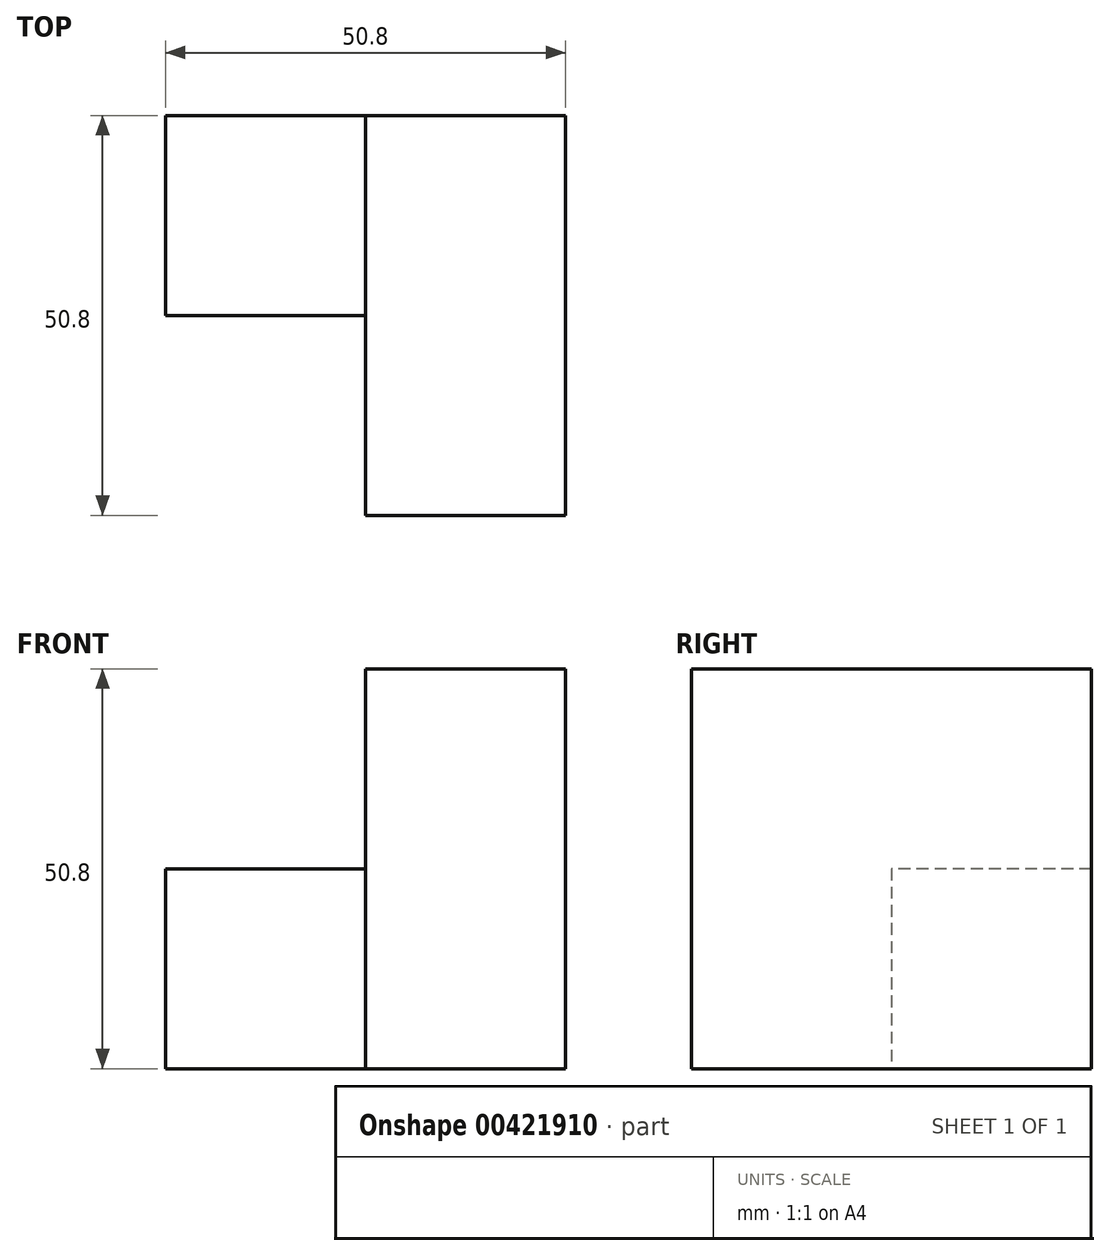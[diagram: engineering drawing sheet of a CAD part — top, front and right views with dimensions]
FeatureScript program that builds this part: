
annotation { "Feature Type Name" : "Feature", "Feature Type Description" : "" }
export const myFeature = defineFeature(function(context is Context, id is Id, definition is map)
    precondition{}
    {
        {
            var Q0;
            Q0=qCreatedBy(makeId("Front.planeOp"),FACE);
            var sketch = newSketch(context, id + "F0", { "sketchPlane" : qUnion([Q0])});
            skLineSegment(sketch, "E0", {"start": v(0, 0) * mm, "end": v(25.4, 0) * mm});
            skLineSegment(sketch, "E1", {"start": v(25.4, 0) * mm, "end": v(25.4, 50.8) * mm});
            skLineSegment(sketch, "E2", {"start": v(25.4, 50.8) * mm, "end": v(0, 50.8) * mm});
            skLineSegment(sketch, "E3", {"start": v(0, 50.8) * mm, "end": v(0, 0) * mm});
            skSolve(sketch);
        }
        {
            var Q0;
            Q0=makeQuery(id+"F0.imprint","IMPRINT",FACE,{"disambiguationData":[TD([[makeQuery(id+"F0.imprint","IMPRINT",EDGE,{"derivedFrom":sQuery(id+"F0.wireOp",EDGE,"E0")}),1.0]])]});
            extrude(context, id + "F1", {"entities" : qUnion([Q0]), "depth" : 50.8 * mm});
        }
        {
            var Q0;
            Q0=qCreatedBy(makeId("Right.planeOp"),FACE);
            var sketch = newSketch(context, id + "F2", { "sketchPlane" : qUnion([Q0])});
            skLineSegment(sketch, "E4", {"start": v(0, 25.4) * mm, "end": v(-25.4, 25.4) * mm});
            skLineSegment(sketch, "E5", {"start": v(-25.4, 25.4) * mm, "end": v(-25.4, 0) * mm});
            skLineSegment(sketch, "E6", {"start": v(0, 0) * mm, "end": v(-25.4, 0) * mm});
            skLineSegment(sketch, "E7", {"start": v(0, 25.4) * mm, "end": v(0, 0) * mm});
            skSolve(sketch);
        }
        {
            var Q0;
            Q0=makeQuery(id+"F2.imprint","IMPRINT",FACE,{"disambiguationData":[TD([[makeQuery(id+"F2.imprint","IMPRINT",EDGE,{"derivedFrom":sQuery(id+"F2.wireOp",EDGE,"E4")}),1.0]])]});
            extrude(context, id + "F3", {"entities" : qUnion([Q0]), "operationType" : NewBodyOperationType.ADD, "oppositeDirection" : true, "depth" : 25.4 * mm});
        }
    });
